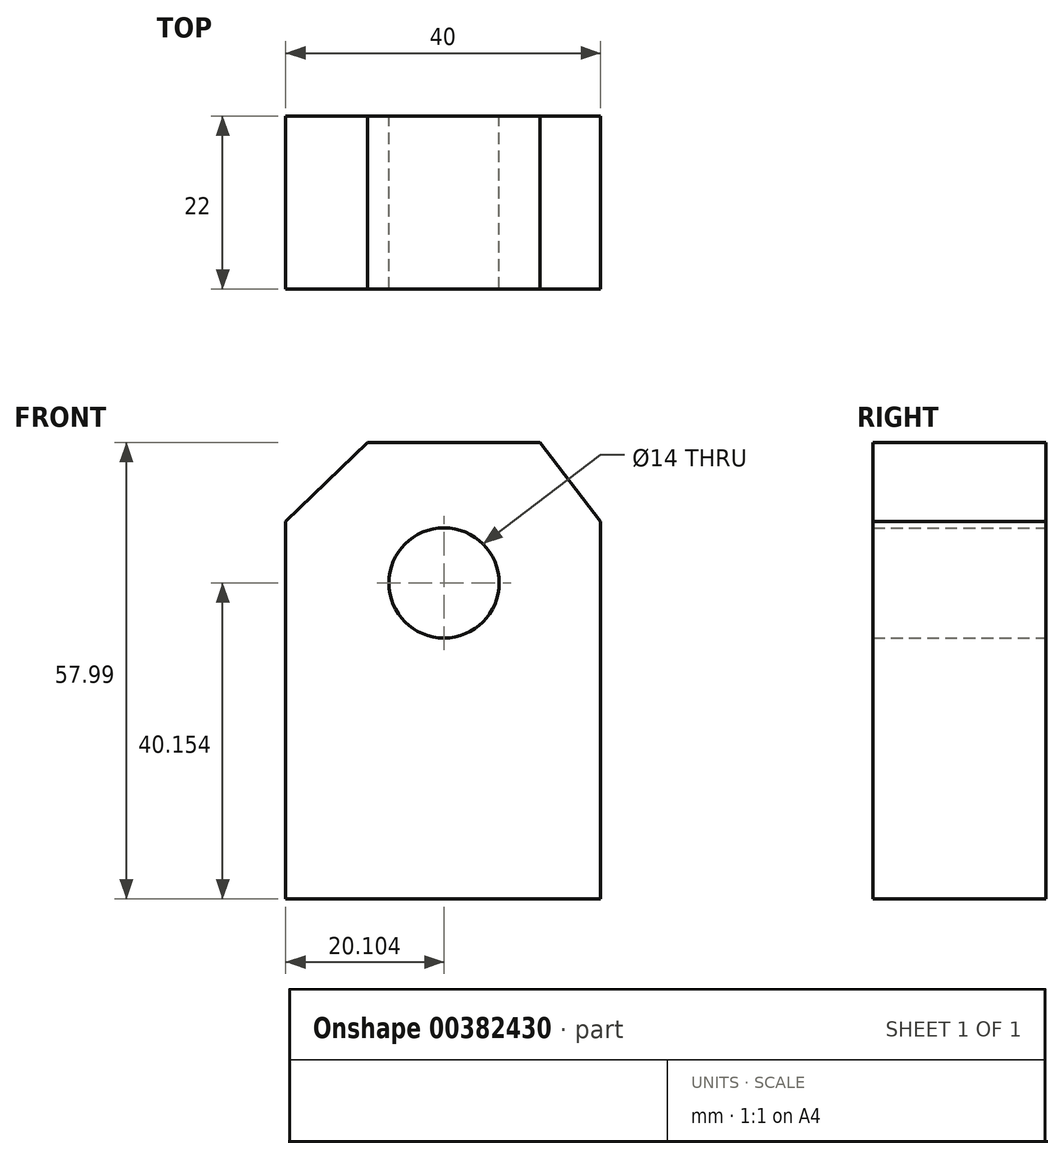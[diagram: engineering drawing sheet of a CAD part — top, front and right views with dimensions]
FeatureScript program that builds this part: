
annotation { "Feature Type Name" : "Feature", "Feature Type Description" : "" }
export const myFeature = defineFeature(function(context is Context, id is Id, definition is map)
    precondition{}
    {
        {
            var Q0;
            Q0=qCreatedBy(makeId("Front.planeOp"),FACE);
            var sketch = newSketch(context, id + "F0", { "sketchPlane" : qUnion([Q0])});
            skLineSegment(sketch, "E0", {"start": v(-32.32, 0) * mm, "end": v(-32.32, -47.98) * mm});
            skLineSegment(sketch, "E1", {"start": v(-32.32, -47.98) * mm, "end": v(7.68, -47.98) * mm});
            skLineSegment(sketch, "E2", {"start": v(7.68, -47.98) * mm, "end": v(7.68, 0) * mm});
            skLineSegment(sketch, "E3", {"start": v(0, 10) * mm, "end": v(-21.92, 10) * mm});
            skLineSegment(sketch, "E4", {"start": v(-32.32, 0) * mm, "end": v(-21.92, 10) * mm});
            skLineSegment(sketch, "E5", {"start": v(7.68, 0) * mm, "end": v(0, 10) * mm});
            skCircle(sketch, "E6", {"center": v(-12.22, -7.83) * mm, "radius": 7 * mm});
            skSolve(sketch);
        }
        {
            var Q0;
            Q0=makeQuery(id+"F0.imprint","IMPRINT",FACE,{"disambiguationData":[TD([[makeQuery(id+"F0.imprint","IMPRINT",EDGE,{"derivedFrom":sQuery(id+"F0.wireOp",EDGE,"E0")}),1.0]])]});
            extrude(context, id + "F1", {"entities" : qUnion([Q0]), "depth" : 22 * mm});
        }
    });
